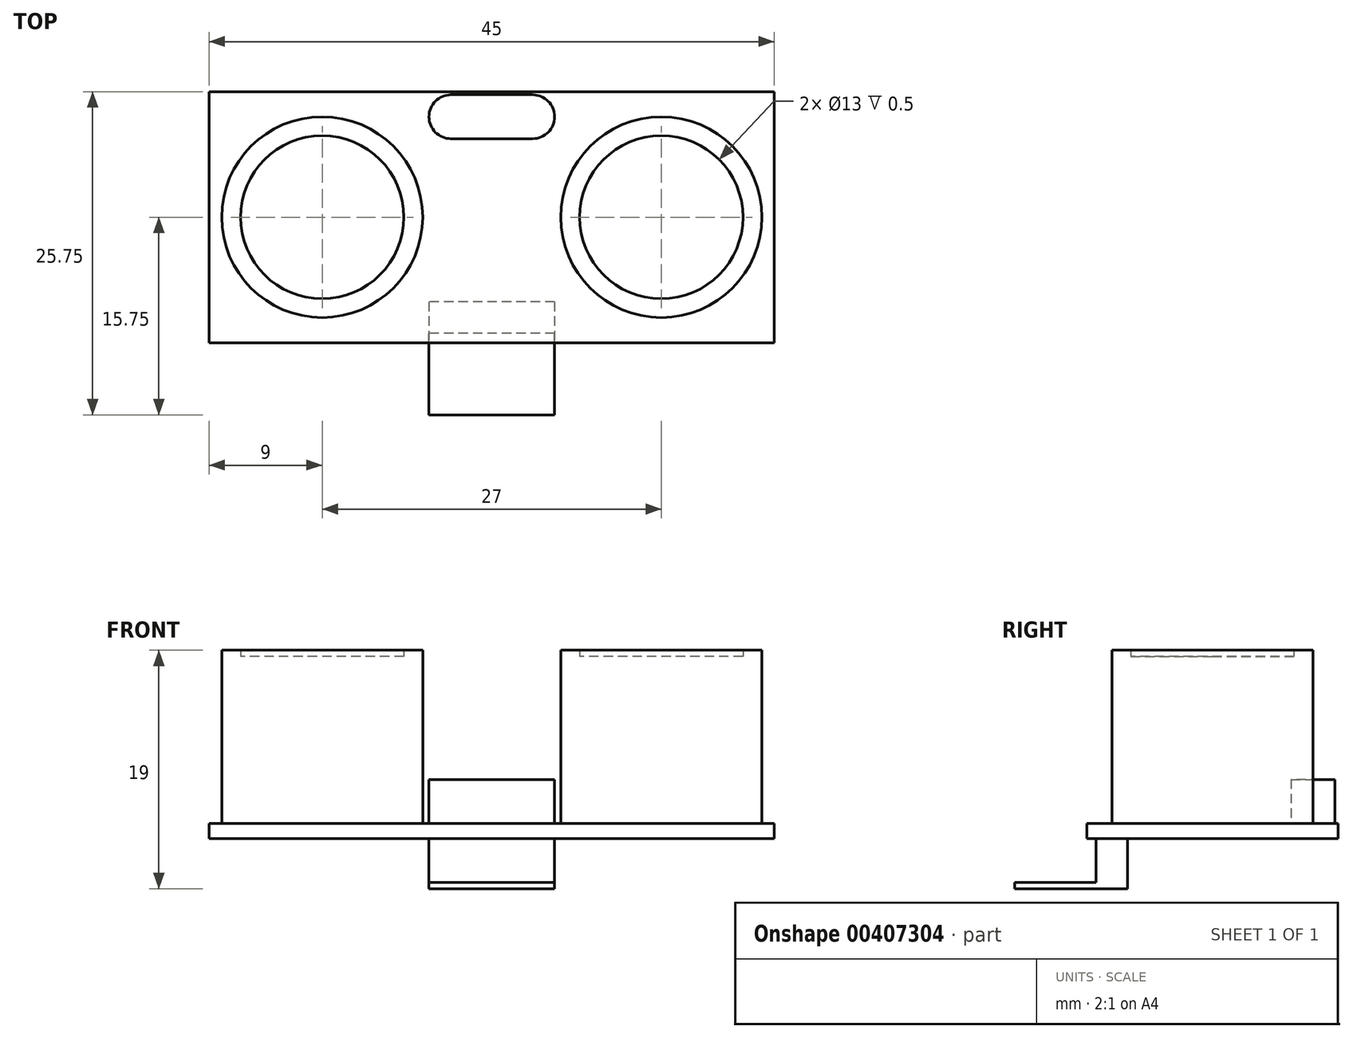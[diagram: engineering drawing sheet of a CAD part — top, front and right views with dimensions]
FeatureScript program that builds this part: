
annotation { "Feature Type Name" : "Feature", "Feature Type Description" : "" }
export const myFeature = defineFeature(function(context is Context, id is Id, definition is map)
    precondition{}
    {
        {
            var Q0;
            Q0=qCreatedBy(makeId("Top.planeOp"),FACE);
            var sketch = newSketch(context, id + "F0", { "sketchPlane" : qUnion([Q0])});
            skLineSegment(sketch, "E0.bottom", {"start": v(0, 0) * mm, "end": v(45, 0) * mm});
            skLineSegment(sketch, "E0.top", {"start": v(0, -20) * mm, "end": v(45, -20) * mm});
            skLineSegment(sketch, "E0.left", {"start": v(0, 0) * mm, "end": v(0, -20) * mm});
            skLineSegment(sketch, "E0.right", {"start": v(45, 0) * mm, "end": v(45, -20) * mm});
            skLineSegment(sketch, "E1", {"start": v(22.5, 0) * mm, "end": v(9, 0) * mm});
            skLineSegment(sketch, "E2", {"start": v(22.5, 0) * mm, "end": v(36, 0) * mm});
            skLineSegment(sketch, "E3", {"start": v(9, 0) * mm, "end": v(9, -10) * mm});
            skPoint(sketch, "E3.endSnap0", {"position": v(0, -10) * mm});
            skLineSegment(sketch, "E4", {"start": v(36, 0) * mm, "end": v(36, -10) * mm});
            skPoint(sketch, "E4.endSnap0", {"position": v(45, -10) * mm});
            skLineSegment(sketch, "E5", {"start": v(22.5, 0) * mm, "end": v(22.5, -2) * mm});
            skPoint(sketch, "E6.middle", {"position": v(22.5, -2) * mm});
            skSolve(sketch);
        }
        {
            var Q0;
            Q0=makeQuery(id+"F0.imprint","IMPRINT",FACE,{"disambiguationData":[TD([[makeQuery(id+"F0.imprint","IMPRINT",EDGE,{"derivedFrom":sQuery(id+"F0.wireOp",EDGE,"E0.top")}),1.0]])]});
            extrude(context, id + "F1", {"entities" : qUnion([Q0]), "depth" : 1.2 * mm});
        }
        {
            var Q0;
            Q0=makeQuery(id+"F1.opExtrude","CAP_FACE",FACE,{"disambiguationData":[OSD([sQuery(id+"F0.wireOp",EDGE,"E0.bottom"),sQuery(id+"F0.wireOp",EDGE,"E0.top"),sQuery(id+"F0.wireOp",EDGE,"E0.left"),sQuery(id+"F0.wireOp",EDGE,"E0.right")])],"isStart":true});
            var sketch = newSketch(context, id + "F2", { "sketchPlane" : qUnion([Q0])});
            skLineSegment(sketch, "E7", {"start": v(0, 0) * mm, "end": v(22.5, 0) * mm});
            skLineSegment(sketch, "E8", {"start": v(22.5, 0) * mm, "end": v(22.5, 18) * mm});
            skPoint(sketch, "E8.endSnap0", {"position": v(22.5, 20) * mm});
            skLineSegment(sketch, "E9.bottom", {"start": v(27.5, 16.75) * mm, "end": v(17.5, 16.75) * mm});
            skLineSegment(sketch, "E9.top", {"start": v(27.5, 19.25) * mm, "end": v(17.5, 19.25) * mm});
            skLineSegment(sketch, "E9.left", {"start": v(27.5, 16.75) * mm, "end": v(27.5, 19.25) * mm});
            skLineSegment(sketch, "E9.right", {"start": v(17.5, 16.75) * mm, "end": v(17.5, 19.25) * mm});
            skPoint(sketch, "E9.middle", {"position": v(22.5, 18) * mm});
            skSolve(sketch);
        }
        {
            var Q0;
            Q0 = qSketchRegion(id + "F2", true);
            extrude(context, id + "F3", {"entities" : qUnion([Q0]), "operationType" : NewBodyOperationType.ADD, "depth" : 4 * mm});
        }
        {
            var Q0;
            Q0=makeQuery(id+"F3.opExtrude","SWEPT_FACE",FACE,{"disambiguationData":[OSD([sQuery(id+"F2.wireOp",EDGE,"E9.top")])]});
            var sketch = newSketch(context, id + "F4", { "sketchPlane" : qUnion([Q0])});
            skLineSegment(sketch, "E10", {"start": v(0, 0) * mm, "end": v(22.5, 0) * mm});
            skLineSegment(sketch, "E11", {"start": v(22.5, 0) * mm, "end": v(22.5, -3.75) * mm});
            skPoint(sketch, "E11.endSnap0", {"position": v(22.5, -4) * mm});
            skLineSegment(sketch, "E12.bottom", {"start": v(17.5, -3.5) * mm, "end": v(27.5, -3.5) * mm});
            skLineSegment(sketch, "E12.top", {"start": v(17.5, -4) * mm, "end": v(27.5, -4) * mm});
            skLineSegment(sketch, "E12.left", {"start": v(17.5, -3.5) * mm, "end": v(17.5, -4) * mm});
            skLineSegment(sketch, "E12.right", {"start": v(27.5, -3.5) * mm, "end": v(27.5, -4) * mm});
            skPoint(sketch, "E12.middle", {"position": v(22.5, -3.75) * mm});
            skSolve(sketch);
        }
        {
            var Q0;
            Q0 = qSketchRegion(id + "F4", true);
            extrude(context, id + "F5", {"entities" : qUnion([Q0]), "operationType" : NewBodyOperationType.ADD, "depth" : 6.5 * mm});
        }
        {
            var Q0;
            Q0=makeQuery(id+"F1.opExtrude","CAP_FACE",FACE,{"disambiguationData":[OSD([sQuery(id+"F0.wireOp",EDGE,"E0.bottom"),sQuery(id+"F0.wireOp",EDGE,"E0.top"),sQuery(id+"F0.wireOp",EDGE,"E0.left"),sQuery(id+"F0.wireOp",EDGE,"E0.right")])],"isStart":false});
            var sketch = newSketch(context, id + "F6", { "sketchPlane" : qUnion([Q0])});
            skLineSegment(sketch, "E13", {"start": v(0, 0) * mm, "end": v(22.5, 0) * mm});
            skLineSegment(sketch, "E14", {"start": v(22.5, 0) * mm, "end": v(9, 0) * mm});
            skLineSegment(sketch, "E15", {"start": v(9, 0) * mm, "end": v(9, -10) * mm});
            skPoint(sketch, "E15.endSnap0", {"position": v(0, -10) * mm});
            skCircle(sketch, "E16", {"center": v(9, -10) * mm, "radius": 8 * mm});
            skCircle(sketch, "E17", {"center": v(9, -10) * mm, "radius": 6.5 * mm});
            skLineSegment(sketch, "E18", {"start": v(9, -10) * mm, "end": v(36, -10) * mm});
            skCircle(sketch, "E19", {"center": v(36, -10) * mm, "radius": 8 * mm});
            skCircle(sketch, "E20", {"center": v(36, -10) * mm, "radius": 6.5 * mm});
            skLineSegment(sketch, "E21", {"start": v(22.5, 0) * mm, "end": v(22.5, -2) * mm});
            skLineSegment(sketch, "E22.bottom", {"start": v(27.5, -0.25) * mm, "end": v(17.5, -0.25) * mm});
            skLineSegment(sketch, "E22.top", {"start": v(27.5, -3.75) * mm, "end": v(17.5, -3.75) * mm});
            skLineSegment(sketch, "E22.left", {"start": v(27.5, -0.25) * mm, "end": v(27.5, -3.75) * mm});
            skLineSegment(sketch, "E22.right", {"start": v(17.5, -0.25) * mm, "end": v(17.5, -3.75) * mm});
            skPoint(sketch, "E22.middle", {"position": v(22.5, -2) * mm});
            skSolve(sketch);
        }
        {
            var Q0;
            Q0=makeQuery(id+"F6.imprint","IMPRINT",FACE,{"disambiguationData":[TD([[makeQuery(id+"F6.imprint","IMPRINT",EDGE,{"derivedFrom":sQuery(id+"F6.wireOp",EDGE,"E19")}),1.0]])]});
            var Q1;
            {var subQ0=sQuery(id+"F6.wireOp",EDGE,"E16");var subQ1=sQuery(id+"F6.wireOp",EDGE,"E15");var subQ2=makeQuery(id+"F6.imprint","INTERSECT",VERTEX,{"derivedFrom":[subQ1,subQ0]});Q1=makeQuery(id+"F6.imprint","IMPRINT",FACE,{"disambiguationData":[TD([[makeQuery(id+"F6.imprint","IMPRINT",EDGE,{"disambiguationData":[TD([[subQ2,-1.0]])],"derivedFrom":subQ1}),1.0]])]});}
            var Q2;
            {var subQ0=sQuery(id+"F6.wireOp",EDGE,"E16");var subQ1=sQuery(id+"F6.wireOp",EDGE,"E15");var subQ2=makeQuery(id+"F6.imprint","INTERSECT",VERTEX,{"derivedFrom":[subQ1,subQ0]});Q2=makeQuery(id+"F6.imprint","IMPRINT",FACE,{"disambiguationData":[TD([[makeQuery(id+"F6.imprint","IMPRINT",EDGE,{"disambiguationData":[TD([[subQ2,-1.0]])],"derivedFrom":subQ1}),-1.0]])]});}
            extrude(context, id + "F7", {"entities" : qUnion([Q0, Q1, Q2]), "operationType" : NewBodyOperationType.ADD, "depth" : 13.8 * mm});
        }
        {
            var Q0;
            Q0=makeQuery(id+"F7.boolean.opBoolean","SPLIT",FACE,{"disambiguationData":[TD([makeQuery(id+"F7.opExtrude","SWEPT_FACE",FACE,{"disambiguationData":[OSD([sQuery(id+"F6.wireOp",EDGE,"E17")])]})])],"derivedFrom":makeQuery(id+"F1.opExtrude","CAP_FACE",FACE,{"disambiguationData":[OSD([sQuery(id+"F0.wireOp",EDGE,"E0.bottom"),sQuery(id+"F0.wireOp",EDGE,"E0.top"),sQuery(id+"F0.wireOp",EDGE,"E0.left"),sQuery(id+"F0.wireOp",EDGE,"E0.right")])],"isStart":false})});
            var Q1;
            Q1=makeQuery(id+"F7.boolean.opBoolean","SPLIT",FACE,{"disambiguationData":[TD([makeQuery(id+"F7.opExtrude","SWEPT_FACE",FACE,{"disambiguationData":[OSD([sQuery(id+"F6.wireOp",EDGE,"E20")])]})])],"derivedFrom":makeQuery(id+"F1.opExtrude","CAP_FACE",FACE,{"disambiguationData":[OSD([sQuery(id+"F0.wireOp",EDGE,"E0.bottom"),sQuery(id+"F0.wireOp",EDGE,"E0.top"),sQuery(id+"F0.wireOp",EDGE,"E0.left"),sQuery(id+"F0.wireOp",EDGE,"E0.right")])],"isStart":false})});
            extrude(context, id + "F8", {"entities" : qUnion([Q0, Q1]), "operationType" : NewBodyOperationType.ADD, "depth" : 13.3 * mm});
        }
        {
            var Q0;
            Q0=makeQuery(id+"F6.imprint","IMPRINT",FACE,{"disambiguationData":[TD([[makeQuery(id+"F6.imprint","IMPRINT",EDGE,{"derivedFrom":sQuery(id+"F6.wireOp",EDGE,"E22.top")}),-1.0]])]});
            extrude(context, id + "F9", {"entities" : qUnion([Q0]), "operationType" : NewBodyOperationType.ADD, "depth" : 3.5 * mm});
        }
        {
            var Q0;
            Q0=makeQuery(id+"F9.opExtrude","SWEPT_EDGE",EDGE,{"disambiguationData":[OSD([sQuery(id+"F6.wireOp",EDGE,"E22.bottom"),sQuery(id+"F6.wireOp",EDGE,"E22.left")])]});
            var Q1;
            Q1=makeQuery(id+"F9.opExtrude","SWEPT_EDGE",EDGE,{"disambiguationData":[OSD([sQuery(id+"F6.wireOp",EDGE,"E22.top"),sQuery(id+"F6.wireOp",EDGE,"E22.left")])]});
            var Q2;
            Q2=makeQuery(id+"F9.opExtrude","SWEPT_EDGE",EDGE,{"disambiguationData":[OSD([sQuery(id+"F6.wireOp",EDGE,"E22.bottom"),sQuery(id+"F6.wireOp",EDGE,"E22.right")])]});
            var Q3;
            Q3=makeQuery(id+"F9.opExtrude","SWEPT_EDGE",EDGE,{"disambiguationData":[OSD([sQuery(id+"F6.wireOp",EDGE,"E22.top"),sQuery(id+"F6.wireOp",EDGE,"E22.right")])]});
            fillet(context, id + "F10", {"entities" : qUnion([Q0, Q1, Q2, Q3]), "radius" : 1.75 * mm, "tangentPropagation" : true, "allowEdgeOverflow" : false});
        }
    });
